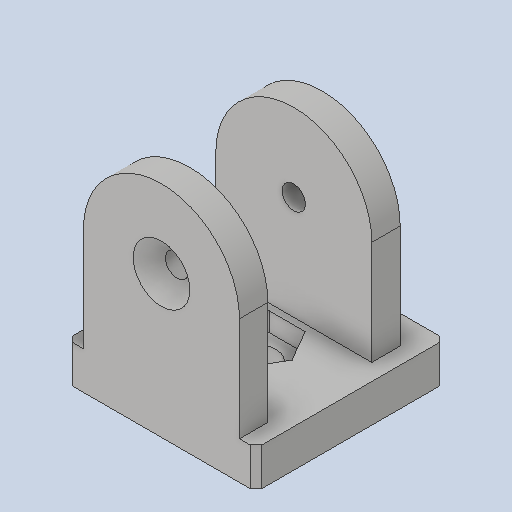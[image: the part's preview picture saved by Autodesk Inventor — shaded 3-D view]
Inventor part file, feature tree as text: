
AUTODESK INVENTOR PART (.ipt)
format: ipt  version: 2023 (Build 270158000, 158)  size: 326,656 bytes
history: native  units: mm
features: other x70, sketch x10, extrude x8, hole x2, chamfer x1
ambient origin geometry x8: Origin, YZ Plane, XZ Plane, XY Plane, X Axis, Y Axis, Z Axis, Center Point
bodies: Solid1 (feature_tree)
feature tree (91):
  extrude  "Extrusion1"  Depth=42.0mm TaperAngle=0.0deg
  extrude  "Extrusion2"  Depth=6.5mm TaperAngle=0.0deg
  extrude  "Extrusion3"  Depth=6.5mm TaperAngle=0.0deg
  hole  "Hole1"  [1 undecoded]
  extrude  "Extrusion4"  TaperAngle=0.0deg  [1 undecoded]
  extrude  "Extrusion5"  TaperAngle=0.0deg  [1 undecoded]
  extrude  "Extrusion6"  TaperAngle=0.0deg  [1 undecoded]
  extrude  "Extrusion7"  TaperAngle=0.0deg  [1 undecoded]
  hole  "Hole2"  [1 undecoded]
  extrude  "Extrusion8"  [1 undecoded]
  other  "GN300Klemmhebel_XY"
  other  "GN300Klemmhebel_YZ"
  other  "GN300Klemmhebel_ZX"
  other  "GN300Klemmhebel_X"
  other  "GN300Klemmhebel_Y"
  other  "GN300Klemmhebel_Z"
  other  "GN300Klemmhebel_Center"
  other  "GUS_4_41_XY"
  other  "GUS_4_41_YZ"
  other  "GUS_4_41_ZX"
  other  "GUS_4_41_X"
  other  "GUS_4_41_Y"
  other  "GUS_4_41_Z"
  other  "GUS_4_41_Center"
  other  "GUS_4_41_L_XY"
  other  "GUS_4_41_L_YZ"
  other  "GUS_4_41_L_ZX"
  other  "GUS_4_41_L_X"
  other  "GUS_4_41_L_Y"
  other  "GUS_4_41_L_Z"
  other  "GUS_4_41_L_Center"
  other  "GUS_4_41_R_XY"
  other  "GUS_4_41_R_YZ"
  other  "GUS_4_41_R_ZX"
  other  "GUS_4_41_R_X"
  other  "GUS_4_41_R_Y"
  other  "GUS_4_41_R_Z"
  other  "GUS_4_41_R_Center"
  other  "p0_XY"
  other  "p0_YZ"
  other  "p0_ZX"
  other  "p0_X"
  other  "p0_Y"
  other  "p0_Z"
  other  "p0_Center"
  other  "p1_XY"
  other  "p1_YZ"
  other  "p1_ZX"
  other  "p1_X"
  other  "p1_Y"
  other  "p1_Z"
  other  "p1_Center"
  other  "p2_XY"
  other  "p2_YZ"
  other  "p2_ZX"
  other  "p2_X"
  other  "p2_Y"
  other  "p2_Z"
  other  "p2_Center"
  other  "p3_XY"
  other  "p3_YZ"
  other  "p3_ZX"
  other  "p3_X"
  other  "p3_Y"
  other  "p3_Z"
  other  "p3_Center"
  other  "p4_XY"
  other  "p4_YZ"
  other  "p4_ZX"
  other  "p4_X"
  other  "p4_Y"
  other  "p4_Z"
  other  "p4_Center"
  other  "ps_XY"
  other  "ps_YZ"
  other  "ps_ZX"
  other  "ps_X"
  other  "ps_Y"
  other  "ps_Z"
  other  "ps_Center"
  chamfer  "Chamfer1"  [1 undecoded]
  sketch  "Skizze_1"  dims[d0=52.0mm d1=0.0mm d2=42.0mm d3=0.0mm]
  sketch  "Skizze_2"  dims[d6=4.92mm d7=6.0mm d8=12.0mm d9=2.0mm d10=16.40943mm d11=39.8mm d12=0.0mm d13=6.5mm d14=0.0mm]
  sketch  "Skizze_3"  dims[d19=6.5mm d20=0.0mm]
  sketch  "Sketch4"  dims[d30=0.0mm d31=0.0mm]
  sketch  "Sketch_1"  dims[d4=42.0mm d5=0.0mm]
  sketch  "Sketch_2"  dims[d15=6.5mm d16=0.0mm d17=6.5mm d18=0.0mm]
  sketch  "Sketch_3"  dims[d21=8.5mm d22=6.0mm d23=4.0mm d24=2.0mm d25=90.0deg d26=8.0mm d27=0.0mm d28=4.0mm d29=0.0mm]
  sketch  "Sketch_4"  dims[d32=0.0mm d33=0.0mm]
  sketch  "Sketch9"  dims[d36=0.0mm d37=0.0mm d38=1.25mm d39=2.0mm d40=45.0deg]
  sketch  "Sketch_5"  dims[d34=0.0mm d35=0.0mm]
note: 8 required parameter values undecoded (feature->parameter linkage not recoverable at this tier; creation-order binding heuristic only, values carry confidence <= 0.55)
